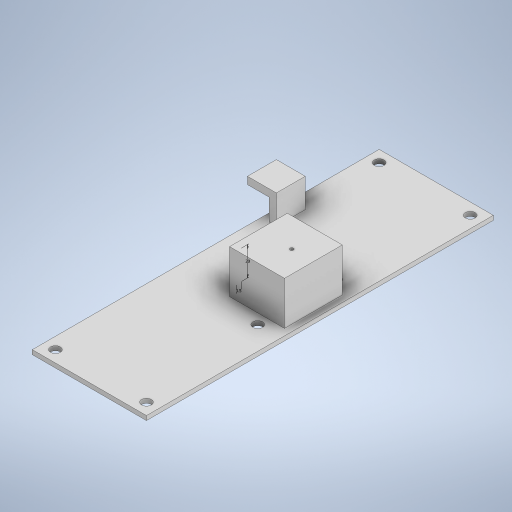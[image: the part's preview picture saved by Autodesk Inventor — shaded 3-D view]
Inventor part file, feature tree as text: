
AUTODESK INVENTOR PART (.ipt)
format: ipt  version: 2023 (Build 270158000, 158)  size: 346,624 bytes
history: native  units: mm
features: sketch x13, extrude x12
ambient origin geometry x8: Origin, YZ Plane, XZ Plane, XY Plane, X Axis, Y Axis, Z Axis, Center Point
bodies: Body1 (feature_tree)
feature tree (25):
  extrude  "Extrusion33"  Depth=240.0mm
  extrude  "Extrusion34"  Depth=38.0mm
  extrude  "Extrusion35"  Depth=30.0mm TaperAngle=0.0deg
  extrude  "Extrusion38"  Depth=30.0mm
  extrude  "Extrusion39"  Depth=15.0mm
  extrude  "Extrusion40"  Depth=3.5mm
  extrude  "Extrusion41"  Depth=35.0mm TaperAngle=0.0deg
  extrude  "Extrusion43"  Depth=20.0mm
  extrude  "Extrusion46"  Depth=20.0mm
  extrude  "Extrusion47"  Depth=5.0mm TaperAngle=0.0deg
  extrude  "Extrusion48"  Depth=10.0mm TaperAngle=0.0deg
  extrude  "Extrusion51"  Depth=6.7mm
  sketch  "Sketch75"  dims[d194=6.7mm d195=6.7mm d196=10.0mm d197=0.0mm d198=6.7mm d199=6.7mm d200=10.0mm d201=0.0mm d202=8.0mm d203=0.0mm d210=2.3mm d211=10.0mm d212=0.0mm d213=3.5mm d214=20.0mm d49=0.5mm d50=0.872665mm d51=0.5mm d52=0.872665mm d130=0.5mm d131=0.872665mm d132=0.5mm d133=0.872665mm d173=0.5mm d174=0.872665mm d175=0.5mm]
  sketch  "Sketch44"  dims[d138=79.0mm d139=240.0mm]
  sketch  "Sketch45"  dims[d140=3.0mm d141=0.0mm d142=38.0mm]
  sketch  "Sketch47"  dims[d143=40.0mm d144=30.0mm d145=0.0mm]
  sketch  "Sketch58"  dims[d146=36.0mm d147=30.0mm d148=-2.617994mm]
  sketch  "Sketch59"  dims[d156=20.0mm d157=15.0mm]
  sketch  "Sketch60"  dims[d158=15.0mm d159=0.0mm d160=3.5mm]
  sketch  "Sketch61"  dims[d161=20.0mm d162=35.0mm d163=0.0mm]
  sketch  "Sketch65"  dims[d164=5.0mm d165=20.0mm]
  sketch  "Sketch68"  dims[d166=20.0mm d167=0.0mm d168=20.0mm]
  sketch  "Sketch69"  dims[d169=20.0mm d170=5.0mm d171=0.0mm]
  sketch  "Sketch70"  dims[d176=6.0mm d177=10.0mm d178=0.0mm]
  sketch  "Sketch74"  dims[d192=6.7mm d193=6.7mm]
